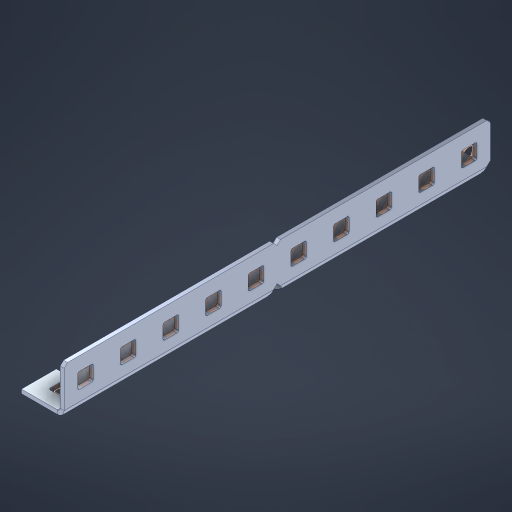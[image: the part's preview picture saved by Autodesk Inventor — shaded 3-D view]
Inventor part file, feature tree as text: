
AUTODESK INVENTOR PART (.ipt)
format: ipt  version: 2023 (Build 270158000, 158)  size: 675,840 bytes
history: native  units: in
note: dims shown in document units (in); Inventor stores cm internally (conversion verified against a paired STEP export)
features: other x37, extrude x28, sheet_metal_op x11, sketch x10, pattern_linear x2, mirror x1, chamfer x1
ambient origin geometry x8: Origin, YZ Plane, XZ Plane, XY Plane, X Axis, Y Axis, Z Axis, Center Point
bodies: Solid1 (feature_tree), Body (feature_tree)
feature tree (90):
  sheet_metal_op  "Flanges"
  other  "Flange Pattern Plane"
  other  "Flange Pattern Sketch"
  sheet_metal_op  "Flange Pattern"
  sheet_metal_op  "Body Pattern"
  pattern_linear  "Center Pattern"  Spacing1=0.0469in  [1 undecoded]
  other  "Arc Length"
  mirror  "Notch Mirror"
  pattern_linear  "Notch Pattern"  Spacing1=0.182in  [1 undecoded]
  chamfer  "End Chamfer"
  extrude  "Half Cut"  Depth=0.02in
  sketch  "Sketch1"  dims[d0=1.0in]
  other  "Plate1"
  sketch  "Sketch2"  dims[d1=5.0in]
  other  "Plate2"
  sheet_metal_op  "Bend1"
  sheet_metal_op  "Corner1"
  sketch  "Sketch3"  dims[d2=0.0469in]
  sketch  "Sketch7"  dims[d3=0.0469in]
  other  "Srf1"
  other  "Srf2"
  sketch  "Sketch8"  dims[d4=0.0234in]
  sketch  "Sketch9"  dims[d5=0.0938in]
  other  "Srf91"
  sheet_metal_op  "Body Pattern Sketch"
  other  "Srf92"
  sketch  "Sketch13"  dims[d6=0.0469in]
  sketch  "Sketch14"  dims[d7=0.5in d8=90.0deg d9=0.0312in]
  sketch  "Sketch15"  dims[d10=0.1875in]
  sketch  "Sketch16"  dims[d11=0.0469in d12=0.0469in d16=0.182in d17=0.02in d18=0.0469in d19=0.0in d20=0.25in d21=0.25in d38=3.937in d40=0.5in d41=0.3937in d43=1.0in d46=0.172in d47=1.0in d48=0.0in d49=0.182in d50=0.02in d51=0.25in d52=0.25in d53=0.0469in d54=0.0in d55=0.172in d56=1.0in d57=0.0in d58=0.25in d60=3.937in d62=0.5in d63=0.3937in d65=0.5in d85=0.1227in d86=0.1659in d88=0.04in d89=0.0469in d90=0.0in d91=0.04in d92=0.0491in d95=2.5in d96=0.04in d97=0.25in d98=45.0deg d99=0.25in d100=0.5in d101=0.0in d102=2.497in d106=0.182in d107=0.02in d108=0.5in d109=0.5in d110=0.0469in d111=0.0in d112=0.172in d113=0.5in d114=0.0in d117=0.5in d118=0.5in d119=0.5in]
  other  "Srf786"
  other  "Srf823"
  other  "Srf824"
  other  "Srf825"
  other  "Srf826"
  other  "Srf827"
  other  "Srf828"
  other  "Srf829"
  other  "Srf856"
  other  "Srf857"
  other  "Srf858"
  other  "Srf859"
  other  "Srf860"
  other  "Srf861"
  other  "Srf862"
  other  "Srf889"
  other  "Srf890"
  other  "Srf891"
  other  "Srf892"
  other  "Srf893"
  other  "Srf894"
  other  "Srf895"
  other  "Srf896"
  other  "Srf922"
  other  "Srf959"
  other  "Srf996"
  sheet_metal_op  "Flange Stamp"
  sheet_metal_op  "Flange Circle"
  sheet_metal_op  "Body Stamp"
  sheet_metal_op  "Body Circle"
  other  "Center Stamp"
  other  "Center Circle"
  sheet_metal_op  "Notch"
  extrude  "ExtrusionSrf2"  Depth=0.0469in
  extrude  "ExtrusionSrf92"  TaperAngle=0.0deg  [1 undecoded]
  extrude  "ExtrusionSrf823"  Depth=0.25in
  extrude  "ExtrusionSrf824"  Depth=0.25in
  extrude  "ExtrusionSrf825"  Depth=0.5in
  extrude  "ExtrusionSrf826"  Depth=0.5in
  extrude  "ExtrusionSrf827"  Depth=1.0in TaperAngle=0.0deg
  extrude  "ExtrusionSrf828"  Depth=0.182in
  extrude  "ExtrusionSrf829"  Depth=0.02in
  extrude  "ExtrusionSrf856"  Depth=0.25in
  extrude  "ExtrusionSrf857"  Depth=0.25in
  extrude  "ExtrusionSrf858"  Depth=0.0469in
  extrude  "ExtrusionSrf859"  TaperAngle=0.0deg  [1 undecoded]
  extrude  "ExtrusionSrf860"  Depth=0.5in
  extrude  "ExtrusionSrf861"  Depth=1.0in TaperAngle=0.0deg
  extrude  "ExtrusionSrf862"  Depth=0.25in
  extrude  "ExtrusionSrf889"  Depth=0.5in
  extrude  "ExtrusionSrf890"  Depth=0.5in
  extrude  "ExtrusionSrf891"  Depth=0.5in
  extrude  "ExtrusionSrf892"  Depth=0.5in
  extrude  "ExtrusionSrf893"  Depth=0.5in
  extrude  "ExtrusionSrf894"  Depth=0.0469in
  extrude  "ExtrusionSrf895"  TaperAngle=0.0deg  [1 undecoded]
  extrude  "ExtrusionSrf896"  Depth=0.5in
  extrude  "ExtrusionSrf922"  Depth=0.5in
  extrude  "ExtrusionSrf959"  Depth=2.5in
  extrude  "ExtrusionSrf996"  Depth=0.25in TaperAngle=45.0deg
note: 5 required parameter values undecoded (feature->parameter linkage not recoverable at this tier; creation-order binding heuristic only, values carry confidence <= 0.55)
